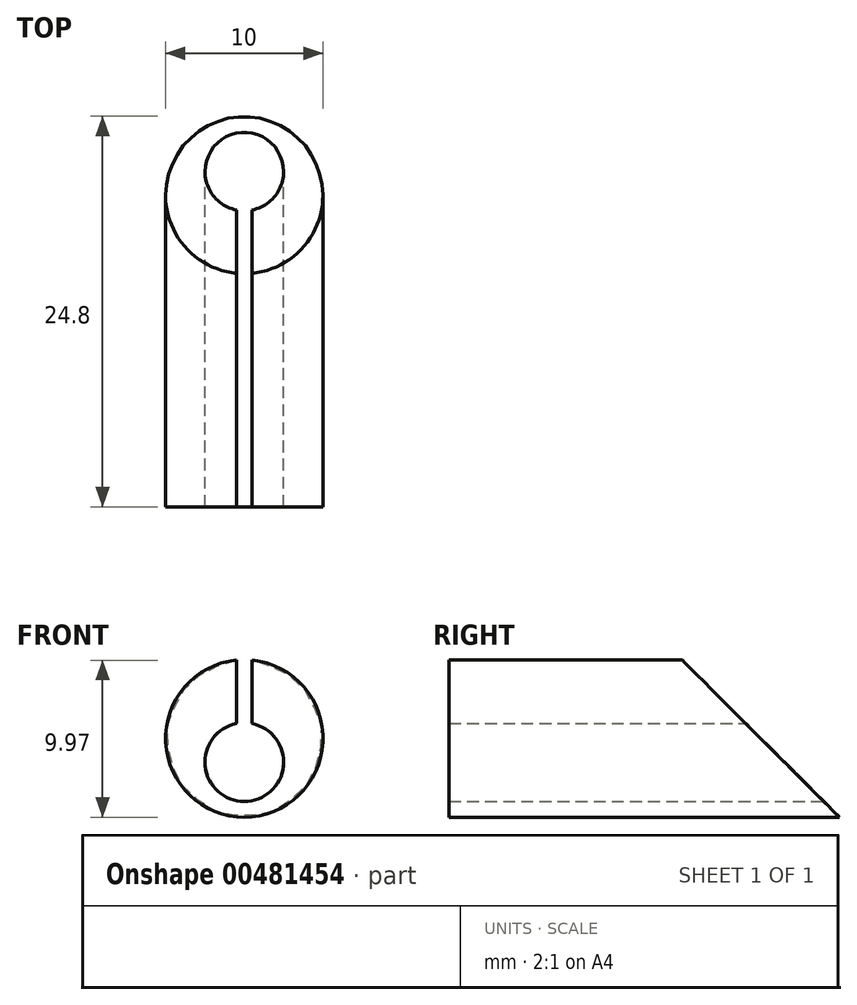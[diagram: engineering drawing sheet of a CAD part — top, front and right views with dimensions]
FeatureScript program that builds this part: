
annotation { "Feature Type Name" : "Feature", "Feature Type Description" : "" }
export const myFeature = defineFeature(function(context is Context, id is Id, definition is map)
    precondition{}
    {
        {
            var Q0;
            Q0=qCreatedBy(makeId("Front.planeOp"),FACE);
            var sketch = newSketch(context, id + "F0", { "sketchPlane" : qUnion([Q0])});
            skArc(sketch, "E0", {"start": v(-0.5, 4.97) * mm, "mid": v(0, -5) * mm, "end": v(0.5, 4.97) * mm});
            skArc(sketch, "E1", {"start": v(-0.5, 0.95) * mm, "mid": v(0, -4) * mm, "end": v(0.5, 0.95) * mm});
            skLineSegment(sketch, "E2.left", {"start": v(-0.5, 4.97) * mm, "end": v(-0.5, 0.95) * mm});
            skLineSegment(sketch, "E2.right", {"start": v(0.5, 4.97) * mm, "end": v(0.5, 0.95) * mm});
            skSolve(sketch);
        }
        {
            var Q0;
            Q0 = qSketchRegion(id + "F0", true);
            extrude(context, id + "F1", {"entities" : qUnion([Q0]), "depth" : 25 * mm});
        }
        {
            var Q0;
            Q0=qCreatedBy(makeId("Right.planeOp"),FACE);
            var sketch = newSketch(context, id + "F2", { "sketchPlane" : qUnion([Q0])});
            skLineSegment(sketch, "E3", {"start": v(-17.5, 12.3) * mm, "end": v(11.28, -16.49) * mm});
            skLineSegment(sketch, "E4", {"start": v(11.28, -16.49) * mm, "end": v(11.28, 12.3) * mm});
            skLineSegment(sketch, "E5", {"start": v(11.28, 12.3) * mm, "end": v(-17.5, 12.3) * mm});
            skSolve(sketch);
        }
        {
            var Q0;
            Q0 = qSketchRegion(id + "F2", true);
            extrude(context, id + "F3", {"entities" : qUnion([Q0]), "operationType" : NewBodyOperationType.REMOVE, "oppositeDirection" : true, "depth" : 25 * mm, "hasSecondDirection" : true, "secondDirectionOppositeDirection" : false, "secondDirectionDepth" : 25 * mm});
        }
    });
